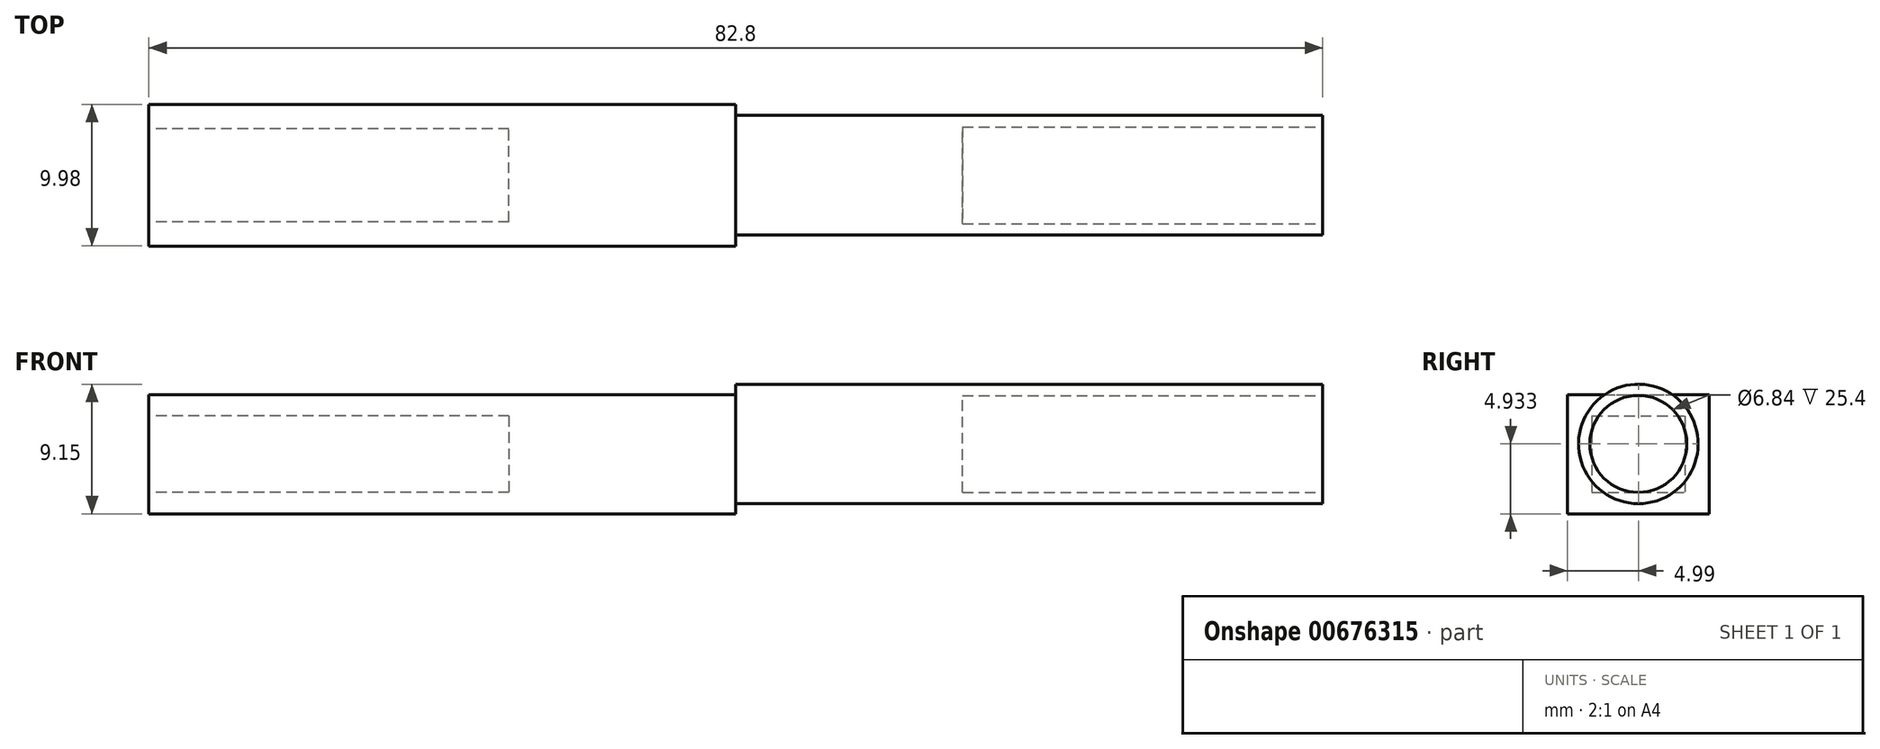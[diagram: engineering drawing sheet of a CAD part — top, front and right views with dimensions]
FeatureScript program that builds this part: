
annotation { "Feature Type Name" : "Feature", "Feature Type Description" : "" }
export const myFeature = defineFeature(function(context is Context, id is Id, definition is map)
    precondition{}
    {
        {
            var Q0;
            Q0=qCreatedBy(makeId("Front.planeOp"),FACE);
            var sketch = newSketch(context, id + "F0", { "sketchPlane" : qUnion([Q0])});
            skLineSegment(sketch, "E0", {"start": v(0, 1.29) * mm, "end": v(41.22, 1.29) * mm});
            skLineSegment(sketch, "E1", {"start": v(41.22, 1.29) * mm, "end": v(41.22, -31.73) * mm});
            skLineSegment(sketch, "E2", {"start": v(41.22, -31.73) * mm, "end": v(0, -31.73) * mm});
            skLineSegment(sketch, "E3", {"start": v(0, 40.45) * mm, "end": v(0, -81.25) * mm});
            skArc(sketch, "E4", {"start": v(0, -42.05) * mm, "mid": v(21.25, -39.43) * mm, "end": v(41.22, -31.73) * mm});
            skArc(sketch, "E5", {"start": v(41.22, 1.29) * mm, "mid": v(21.88, 11.88) * mm, "end": v(0, 14.72) * mm});
            skSolve(sketch);
        }
        {
            var Q0;
            Q0=sQuery(id+"F0.wireOp",EDGE,"E5");
            var Q1;
            Q1=sQuery(id+"F0.wireOp",EDGE,"E1");
            var Q2;
            Q2=sQuery(id+"F0.wireOp",EDGE,"E4");
            var Q3;
            Q3=sQuery(id+"F0.wireOp",EDGE,"E3");
            revolve(context, id + "F1", {"bodyType" : ToolBodyType.SURFACE, "surfaceEntities" : qUnion([Q0, Q1, Q2]), "axis" : qUnion([Q3]), "revolveType" : RevolveType.FULL});
        }
        {
            var Q0;
            Q0=qCreatedBy(makeId("Right.planeOp"),FACE);
            var sketch = newSketch(context, id + "F2", { "sketchPlane" : qUnion([Q0])});
            skCircle(sketch, "E6", {"center": v(0, -23.19) * mm, "radius": 4.22 * mm});
            skSolve(sketch);
        }
        {
            var Q0;
            Q0 = qSketchRegion(id + "F2", true);
            extrude(context, id + "F3", {"entities" : qUnion([Q0]), "depth" : 41.4 * mm, "offsetDistance" : 25.4 * mm});
        }
        {
            var Q0;
            Q0=makeQuery(id+"F3.opExtrude","CAP_FACE",FACE,{"disambiguationData":[OSD([sQuery(id+"F2.wireOp",EDGE,"E6")])],"isStart":false});
            var sketch = newSketch(context, id + "F4", { "sketchPlane" : qUnion([Q0])});
            skCircle(sketch, "E7", {"center": v(0, -23.19) * mm, "radius": 3.42 * mm});
            skSolve(sketch);
        }
        {
            var Q0;
            Q0=makeQuery(id+"F4.imprint","IMPRINT",FACE,{"disambiguationData":[TD([[makeQuery(id+"F4.imprint","IMPRINT",EDGE,{"derivedFrom":sQuery(id+"F4.wireOp",EDGE,"E7")}),1.0]])]});
            extrude(context, id + "F5", {"entities" : qUnion([Q0]), "operationType" : NewBodyOperationType.REMOVE, "oppositeDirection" : true, "depth" : 25.4 * mm, "offsetDistance" : 25.4 * mm});
        }
        {
            var Q0;
            Q0=qCreatedBy(makeId("Right.planeOp"),FACE);
            var sketch = newSketch(context, id + "F6", { "sketchPlane" : qUnion([Q0])});
            skLineSegment(sketch, "E8.bottom", {"start": v(-5, -19.7) * mm, "end": v(5, -19.7) * mm});
            skLineSegment(sketch, "E8.top", {"start": v(-5, -28.12) * mm, "end": v(5, -28.12) * mm});
            skLineSegment(sketch, "E8.left", {"start": v(-5, -19.7) * mm, "end": v(-5, -28.12) * mm});
            skLineSegment(sketch, "E8.right", {"start": v(5, -19.7) * mm, "end": v(5, -28.12) * mm});
            skPoint(sketch, "E8.middle", {"position": v(0, -23.91) * mm});
            skSolve(sketch);
        }
        {
            var Q0;
            Q0 = qSketchRegion(id + "F6", true);
            extrude(context, id + "F7", {"entities" : qUnion([Q0]), "operationType" : NewBodyOperationType.ADD, "oppositeDirection" : true, "depth" : 41.4 * mm, "offsetDistance" : 25.4 * mm});
        }
        {
            var Q0;
            Q0=makeQuery(id+"F7.opExtrude","CAP_FACE",FACE,{"disambiguationData":[OSD([sQuery(id+"F6.wireOp",EDGE,"E8.bottom"),sQuery(id+"F6.wireOp",EDGE,"E8.top"),sQuery(id+"F6.wireOp",EDGE,"E8.left"),sQuery(id+"F6.wireOp",EDGE,"E8.right")])],"isStart":false});
            var sketch = newSketch(context, id + "F8", { "sketchPlane" : qUnion([Q0])});
            skLineSegment(sketch, "E9.bottom", {"start": v(3.29, -21.21) * mm, "end": v(-3.29, -21.21) * mm});
            skLineSegment(sketch, "E9.top", {"start": v(3.29, -26.6) * mm, "end": v(-3.29, -26.6) * mm});
            skLineSegment(sketch, "E9.left", {"start": v(3.29, -21.21) * mm, "end": v(3.29, -26.6) * mm});
            skLineSegment(sketch, "E9.right", {"start": v(-3.29, -21.21) * mm, "end": v(-3.29, -26.6) * mm});
            skPoint(sketch, "E9.middle", {"position": v(0, -23.91) * mm});
            skPoint(sketch, "E9.middle.positionSnap0", {"position": v(5, -23.91) * mm});
            skPoint(sketch, "E9.centerSnap0", {"position": v(5, -23.91) * mm});
            skSolve(sketch);
        }
        {
            var Q0;
            Q0 = qSketchRegion(id + "F8", true);
            extrude(context, id + "F9", {"entities" : qUnion([Q0]), "operationType" : NewBodyOperationType.REMOVE, "oppositeDirection" : true, "depth" : 25.4 * mm, "offsetDistance" : 25.4 * mm});
        }
    });
